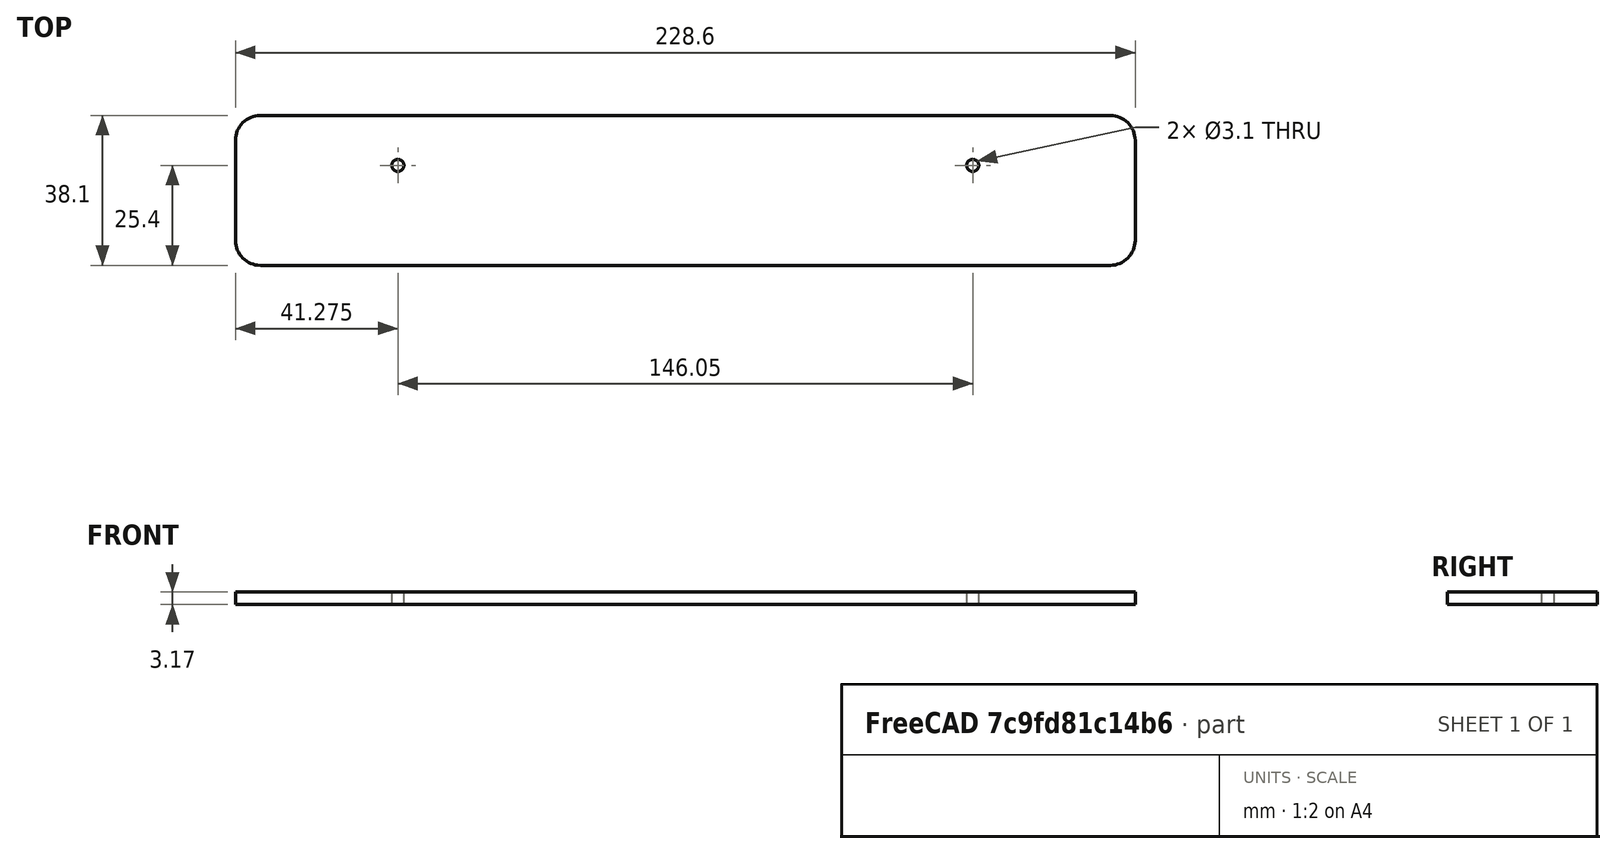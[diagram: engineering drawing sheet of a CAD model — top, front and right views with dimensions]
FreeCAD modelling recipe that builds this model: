
FCSTD DOCUMENT  (FreeCAD 0.19R22756 (Git))
Label: X21_Foot0
License: All rights reserved
LicenseURL: http://en.wikipedia.org/wiki/All_rights_reserved
objects: Sketcher::SketchObject×1, PartDesign::Pad×1, PartDesign::Body×1, PartDesign::CoordinateSystem×1, App::Part×1
note: 5 computed .brp shape members not serialized (recipe doc carries the construction recipe); baked Part::Feature solids carry a one-line shape summary decoded from their .brp

FEATURE [Sketcher::SketchObject] Sketch
  MapMode = 5
  Support = -> [XY_Plane]
  sketch-geometry (11):
    g0: LineSegment StartX=-107.95 StartY=19.05 StartZ=0 EndX=107.95 EndY=19.05 EndZ=0
    g1: LineSegment StartX=114.3 StartY=12.7 StartZ=0 EndX=114.3 EndY=-12.7 EndZ=0
    g2: LineSegment StartX=107.95 StartY=-19.05 StartZ=0 EndX=-107.95 EndY=-19.05 EndZ=0
    g3: LineSegment StartX=-114.3 StartY=-12.7 StartZ=0 EndX=-114.3 EndY=12.7 EndZ=0
    g4: ArcOfCircle CenterX=-107.95 CenterY=12.7 CenterZ=0 NormalX=0 NormalY=0 NormalZ=1 AngleXU=0 Radius=6.35 StartAngle=1.5708 EndAngle=3.14159
    g5: ArcOfCircle CenterX=-107.95 CenterY=-12.7 CenterZ=0 NormalX=0 NormalY=0 NormalZ=1 AngleXU=0 Radius=6.35 StartAngle=3.14159 EndAngle=4.71239
    g6: ArcOfCircle CenterX=107.95 CenterY=-12.7 CenterZ=0 NormalX=0 NormalY=0 NormalZ=1 AngleXU=0 Radius=6.35 StartAngle=4.71239 EndAngle=6.28319
    g7: ArcOfCircle CenterX=107.95 CenterY=12.7 CenterZ=0 NormalX=0 NormalY=0 NormalZ=1 AngleXU=0 Radius=6.35 StartAngle=0 EndAngle=1.5708
    g8: Circle CenterX=-73.025 CenterY=6.35 CenterZ=0 NormalX=0 NormalY=0 NormalZ=1 AngleXU=0 Radius=1.55
    g9: Circle CenterX=73.025 CenterY=6.35 CenterZ=0 NormalX=0 NormalY=0 NormalZ=1 AngleXU=0 Radius=1.55
    g10: LineSegment [constr] StartX=0 StartY=0 StartZ=0 EndX=0 EndY=6.35 EndZ=0
  constraints (27):
    c: Horizontal(g0)
    c: Horizontal(g2)
    c: Vertical(g1)
    c: Vertical(g3)
    c: Tangent(g0,g4) = 1.5708
    c: Tangent(g3,g4) = 1.5708
    c: Tangent(g2,g5) = 1.5708
    c: Tangent(g3,g5) = 1.5708
    c: Tangent(g2,g6) = 1.5708
    c: Tangent(g1,g6) = 1.5708
    c: Tangent(g1,g7) = 1.5708
    c: Tangent(g0,g7) = 1.5708
    c: DistanceX(g3,g1) = 228.6
    c: Equal(g4,g5)
    c: Equal(g5,g6)
    c: Equal(g6,g7)
    c: Radius(g4) = 6.35
    c: Symmetric(g4,g6,g-1)
    c: DistanceY(g2,g0) = 38.1
    c: Equal(g8,g9)
    c: DistanceX(g8,g9) = 146.05
    c: Diameter(g8) = 3.1
    c: Coincident(g10,g-1)
    c: PointOnObject(g10,g-2)
    c: DistanceY(g10,g10) = 6.35
    c: Horizontal(g8,g10)
    c: Symmetric(g8,g9,g10)
FEATURE [PartDesign::Pad] Pad
  Direction = (1,1,1)
  Length = 3.175
  Length2 = 99.9998
  Profile = -> Sketch
  Type = 0
FEATURE [PartDesign::Body] Body
  Group = -> [Sketch,Pad]
  Origin = -> Origin
  Tip = -> Pad
FEATURE [PartDesign::CoordinateSystem] LCS_0
  AttacherType = Attacher::AttachEngine3D
  MapMode = 2
  Support = -> [X_Axis001]
FEATURE [App::Part] Part
  Group = -> [LCS_0,Body]
  Origin = -> Origin001
